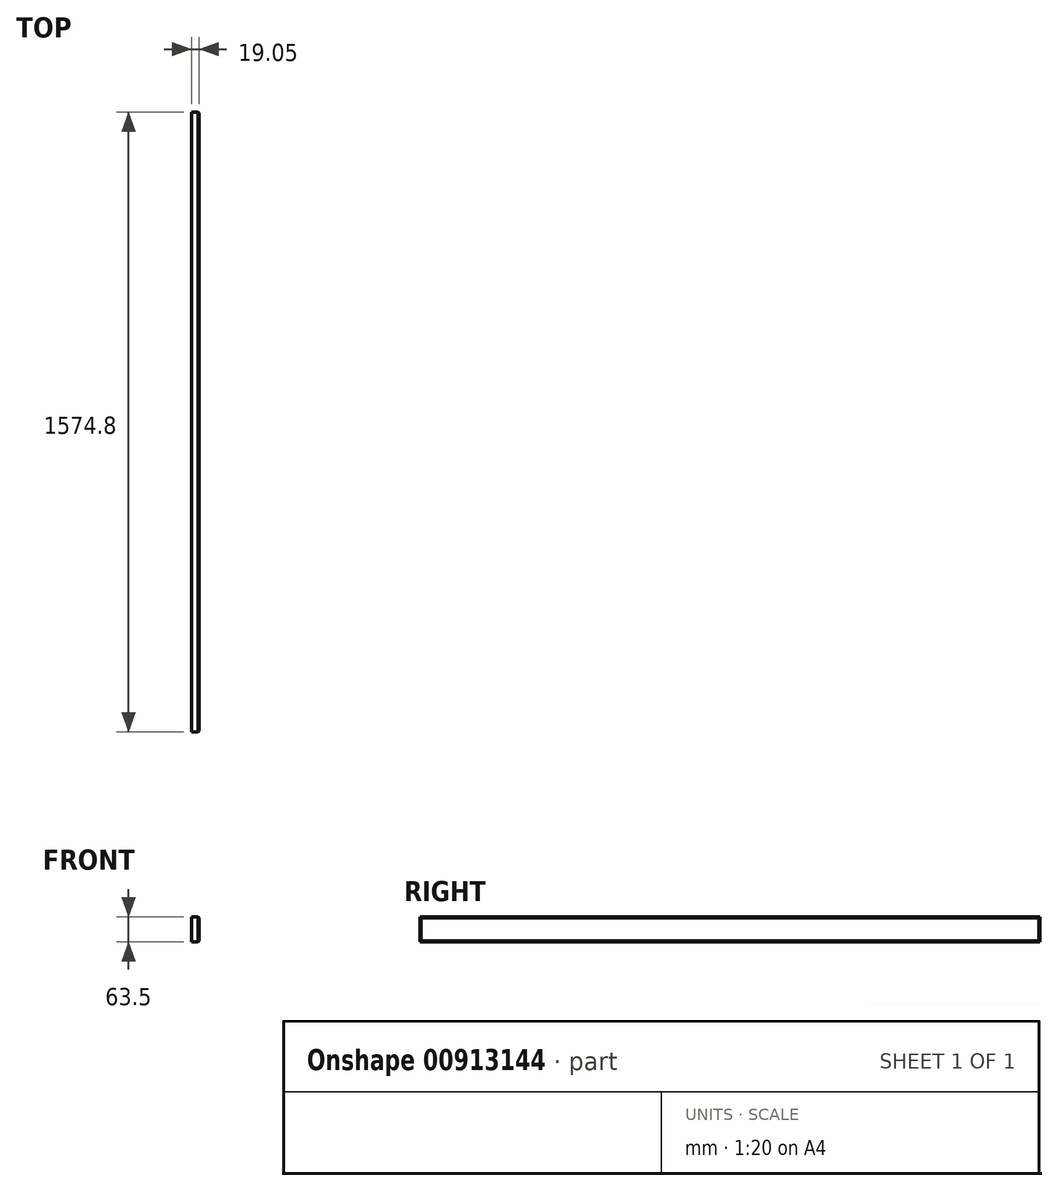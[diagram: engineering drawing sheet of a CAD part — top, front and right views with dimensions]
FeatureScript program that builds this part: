
annotation { "Feature Type Name" : "Feature", "Feature Type Description" : "" }
export const myFeature = defineFeature(function(context is Context, id is Id, definition is map)
    precondition{}
    {
        {
            var Q0;
            Q0=qCreatedBy(makeId("Right.planeOp"),FACE);
            var sketch = newSketch(context, id + "F0", { "sketchPlane" : qUnion([Q0])});
            skLineSegment(sketch, "E0.bottom", {"start": v(-829.04, 13.88) * mm, "end": v(745.76, 13.88) * mm});
            skLineSegment(sketch, "E0.top", {"start": v(-829.04, -49.62) * mm, "end": v(745.76, -49.62) * mm});
            skLineSegment(sketch, "E0.left", {"start": v(-829.04, 13.88) * mm, "end": v(-829.04, -49.62) * mm});
            skLineSegment(sketch, "E0.right", {"start": v(745.76, 13.88) * mm, "end": v(745.76, -49.62) * mm});
            skSolve(sketch);
        }
        {
            var Q0;
            Q0 = qSketchRegion(id + "F0", true);
            extrude(context, id + "F1", {"entities" : qUnion([Q0]), "depth" : 19.05 * mm, "offsetDistance" : 25.4 * mm});
        }
        {
            var Q0;
            Q0=makeQuery(id+"F1.opExtrude","CAP_EDGE",EDGE,{"disambiguationData":[OSD([sQuery(id+"F0.wireOp",EDGE,"E0.bottom")])],"isStart":false});
            var Q1;
            Q1=makeQuery(id+"F1.opExtrude","CAP_EDGE",EDGE,{"disambiguationData":[OSD([sQuery(id+"F0.wireOp",EDGE,"E0.left")])],"isStart":false});
            var Q2;
            Q2=makeQuery(id+"F1.opExtrude","CAP_EDGE",EDGE,{"disambiguationData":[OSD([sQuery(id+"F0.wireOp",EDGE,"E0.top")])],"isStart":false});
            var Q3;
            Q3=makeQuery(id+"F1.opExtrude","CAP_EDGE",EDGE,{"disambiguationData":[OSD([sQuery(id+"F0.wireOp",EDGE,"E0.right")])],"isStart":false});
            chamfer(context, id + "F2", {"entities" : qUnion([Q0, Q1, Q2, Q3]), "width" : 2.54 * mm, "tangentPropagation" : true});
        }
    });
